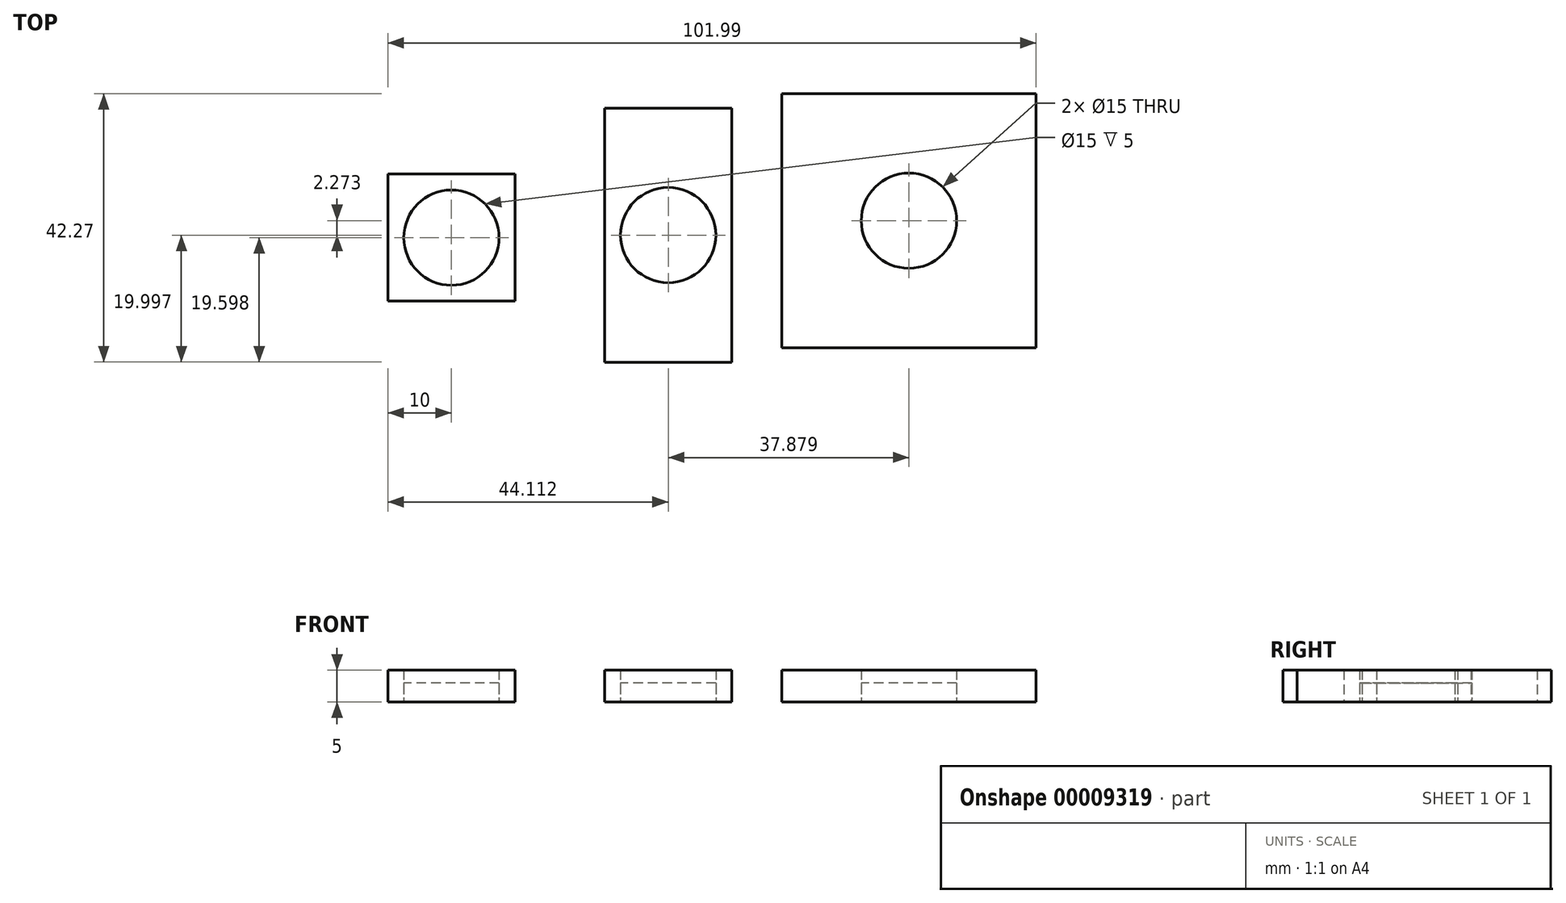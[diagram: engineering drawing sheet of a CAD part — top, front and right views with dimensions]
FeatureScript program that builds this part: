
annotation { "Feature Type Name" : "Feature", "Feature Type Description" : "" }
export const myFeature = defineFeature(function(context is Context, id is Id, definition is map)
    precondition{}
    {
        {
            var Q0;
            Q0=qCreatedBy(makeId("Top.planeOp"),FACE);
            var sketch = newSketch(context, id + "F0", { "sketchPlane" : qUnion([Q0])});
            skLineSegment(sketch, "E0.rect.bottom", {"start": v(-36.15, 41.64) * mm, "end": v(-56.15, 41.64) * mm});
            skLineSegment(sketch, "E0.rect.top", {"start": v(-36.15, 61.64) * mm, "end": v(-56.15, 61.64) * mm});
            skLineSegment(sketch, "E0.rect.left", {"start": v(-36.15, 41.64) * mm, "end": v(-36.15, 61.64) * mm});
            skLineSegment(sketch, "E0.rect.right", {"start": v(-56.15, 41.64) * mm, "end": v(-56.15, 61.64) * mm});
            skPoint(sketch, "E0.rect.middle", {"position": v(-46.15, 51.64) * mm});
            skLineSegment(sketch, "E1.rect.bottom", {"start": v(-2.04, 32.04) * mm, "end": v(-22.04, 32.04) * mm});
            skLineSegment(sketch, "E1.rect.top", {"start": v(-2.04, 72.04) * mm, "end": v(-22.04, 72.04) * mm});
            skLineSegment(sketch, "E1.rect.left", {"start": v(-2.04, 32.04) * mm, "end": v(-2.04, 72.04) * mm});
            skLineSegment(sketch, "E1.rect.right", {"start": v(-22.04, 32.04) * mm, "end": v(-22.04, 72.04) * mm});
            skPoint(sketch, "E1.rect.middle", {"position": v(-12.04, 52.04) * mm});
            skLineSegment(sketch, "E2.rect.bottom", {"start": v(5.84, 74.3) * mm, "end": v(45.84, 74.3) * mm});
            skLineSegment(sketch, "E2.rect.top", {"start": v(5.84, 34.3) * mm, "end": v(45.84, 34.3) * mm});
            skLineSegment(sketch, "E2.rect.left", {"start": v(5.84, 74.3) * mm, "end": v(5.84, 34.3) * mm});
            skLineSegment(sketch, "E2.rect.right", {"start": v(45.84, 74.3) * mm, "end": v(45.84, 34.3) * mm});
            skPoint(sketch, "E2.rect.middle", {"position": v(25.84, 54.3) * mm});
            skCircle(sketch, "E3", {"center": v(-46.15, 51.64) * mm, "radius": 7.5 * mm});
            skCircle(sketch, "E4", {"center": v(-12.04, 52.04) * mm, "radius": 7.5 * mm});
            skCircle(sketch, "E5", {"center": v(25.84, 54.3) * mm, "radius": 7.5 * mm});
            skSolve(sketch);
        }
        {
            var Q0;
            Q0=makeQuery(id+"F0.imprint","IMPRINT",FACE,{"disambiguationData":[TD([[makeQuery(id+"F0.imprint","IMPRINT",EDGE,{"derivedFrom":sQuery(id+"F0.wireOp",EDGE,"E3")}),1.0]])]});
            var Q1;
            Q1=makeQuery(id+"F0.imprint","IMPRINT",FACE,{"disambiguationData":[TD([[makeQuery(id+"F0.imprint","IMPRINT",EDGE,{"derivedFrom":sQuery(id+"F0.wireOp",EDGE,"E4")}),1.0]])]});
            var Q2;
            Q2=makeQuery(id+"F0.imprint","IMPRINT",FACE,{"disambiguationData":[TD([[makeQuery(id+"F0.imprint","IMPRINT",EDGE,{"derivedFrom":sQuery(id+"F0.wireOp",EDGE,"E5")}),1.0]])]});
            extrude(context, id + "F1", {"entities" : qUnion([Q0, Q1, Q2]), "depth" : 3 * mm});
        }
        {
            var Q0;
            Q0=makeQuery(id+"F0.imprint","IMPRINT",FACE,{"disambiguationData":[TD([[makeQuery(id+"F0.imprint","IMPRINT",EDGE,{"derivedFrom":sQuery(id+"F0.wireOp",EDGE,"E0.rect.bottom")}),-1.0]])]});
            var Q1;
            Q1=makeQuery(id+"F0.imprint","IMPRINT",FACE,{"disambiguationData":[TD([[makeQuery(id+"F0.imprint","IMPRINT",EDGE,{"derivedFrom":sQuery(id+"F0.wireOp",EDGE,"E1.rect.bottom")}),-1.0]])]});
            var Q2;
            Q2=makeQuery(id+"F0.imprint","IMPRINT",FACE,{"disambiguationData":[TD([[makeQuery(id+"F0.imprint","IMPRINT",EDGE,{"derivedFrom":sQuery(id+"F0.wireOp",EDGE,"E2.rect.bottom")}),-1.0]])]});
            extrude(context, id + "F2", {"entities" : qUnion([Q0, Q1, Q2]), "depth" : 5 * mm});
        }
    });
